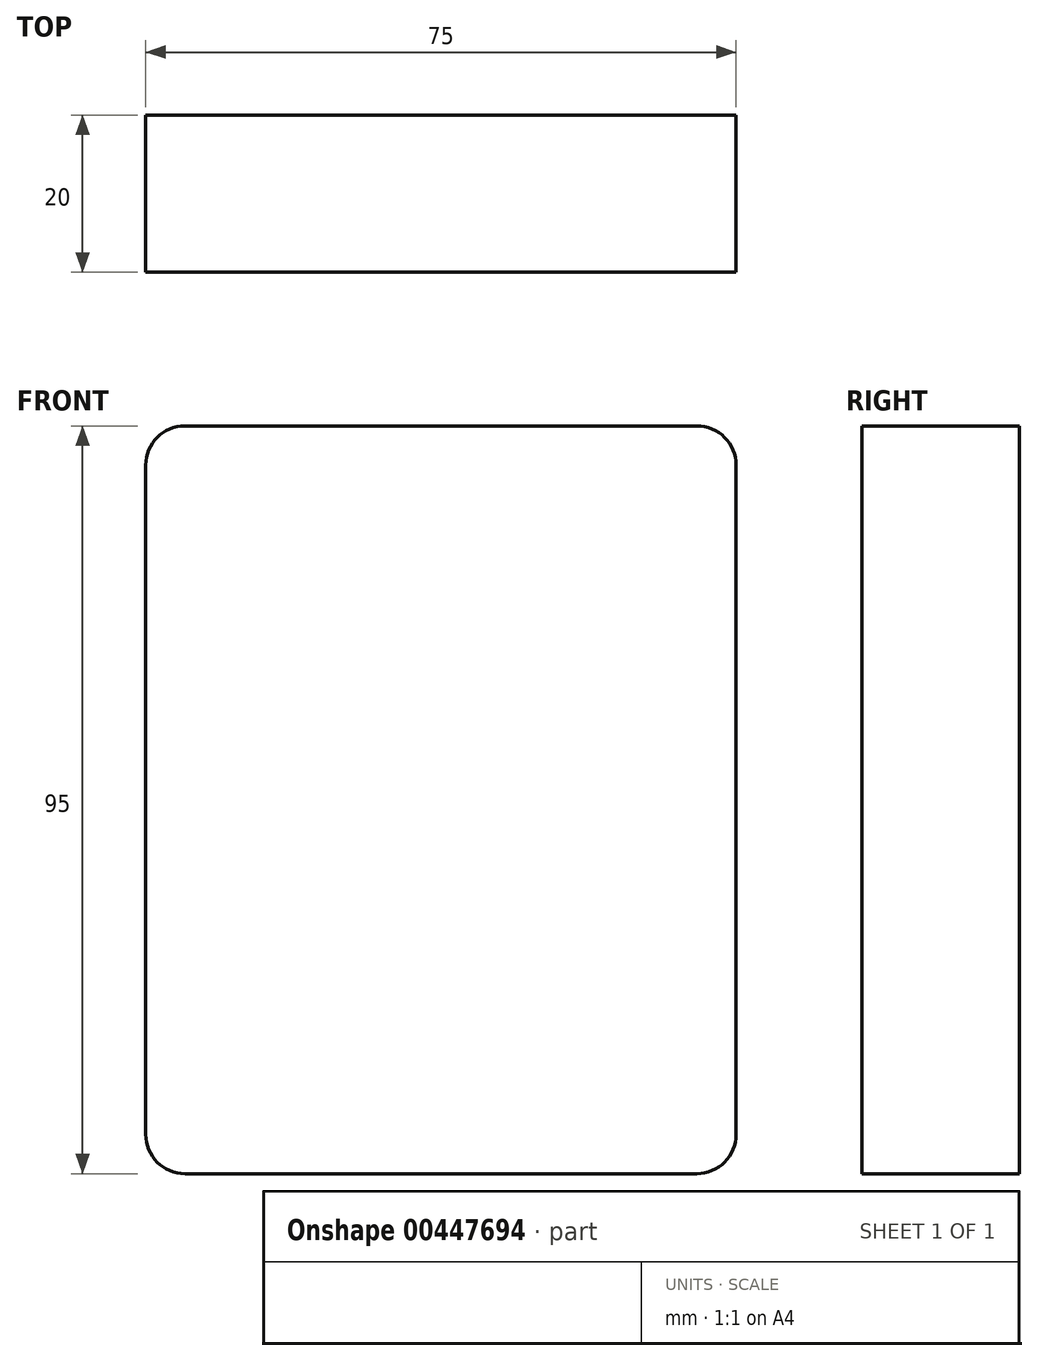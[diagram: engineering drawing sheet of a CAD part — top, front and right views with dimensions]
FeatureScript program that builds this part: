
annotation { "Feature Type Name" : "Feature", "Feature Type Description" : "" }
export const myFeature = defineFeature(function(context is Context, id is Id, definition is map)
    precondition{}
    {
        {
            var Q0;
            Q0=qCreatedBy(makeId("Front.planeOp"),FACE);
            var sketch = newSketch(context, id + "F0", { "sketchPlane" : qUnion([Q0])});
            skLineSegment(sketch, "E0.bottom", {"start": v(-70, 95) * mm, "end": v(-5, 95) * mm});
            skLineSegment(sketch, "E0.top", {"start": v(-70, 0) * mm, "end": v(-5, 0) * mm});
            skLineSegment(sketch, "E0.left", {"start": v(-75, 90) * mm, "end": v(-75, 5) * mm});
            skLineSegment(sketch, "E0.right", {"start": v(0, 90) * mm, "end": v(0, 5) * mm});
            skPoint(sketch, "E1.visualSharp", {"position": v(0, 95) * mm});
            skArc(sketch, "E1.filletArc", {"start": v(0, 90) * mm, "mid": v(-1.46, 93.54) * mm, "end": v(-5, 95) * mm});
            skPoint(sketch, "E2.visualSharp", {"position": v(0, 0) * mm});
            skArc(sketch, "E2.filletArc", {"start": v(-5, 0) * mm, "mid": v(-1.46, 1.46) * mm, "end": v(0, 5) * mm});
            skPoint(sketch, "E3.visualSharp", {"position": v(-75, 0) * mm});
            skArc(sketch, "E3.filletArc", {"start": v(-75, 5) * mm, "mid": v(-73.54, 1.46) * mm, "end": v(-70, 0) * mm});
            skPoint(sketch, "E4.visualSharp", {"position": v(-75, 95) * mm});
            skArc(sketch, "E4.filletArc", {"start": v(-70, 95) * mm, "mid": v(-73.54, 93.54) * mm, "end": v(-75, 90) * mm});
            skSolve(sketch);
        }
        {
            var Q0;
            Q0 = qSketchRegion(id + "F0", true);
            extrude(context, id + "F1", {"entities" : qUnion([Q0]), "depth" : 20 * mm});
        }
    });
